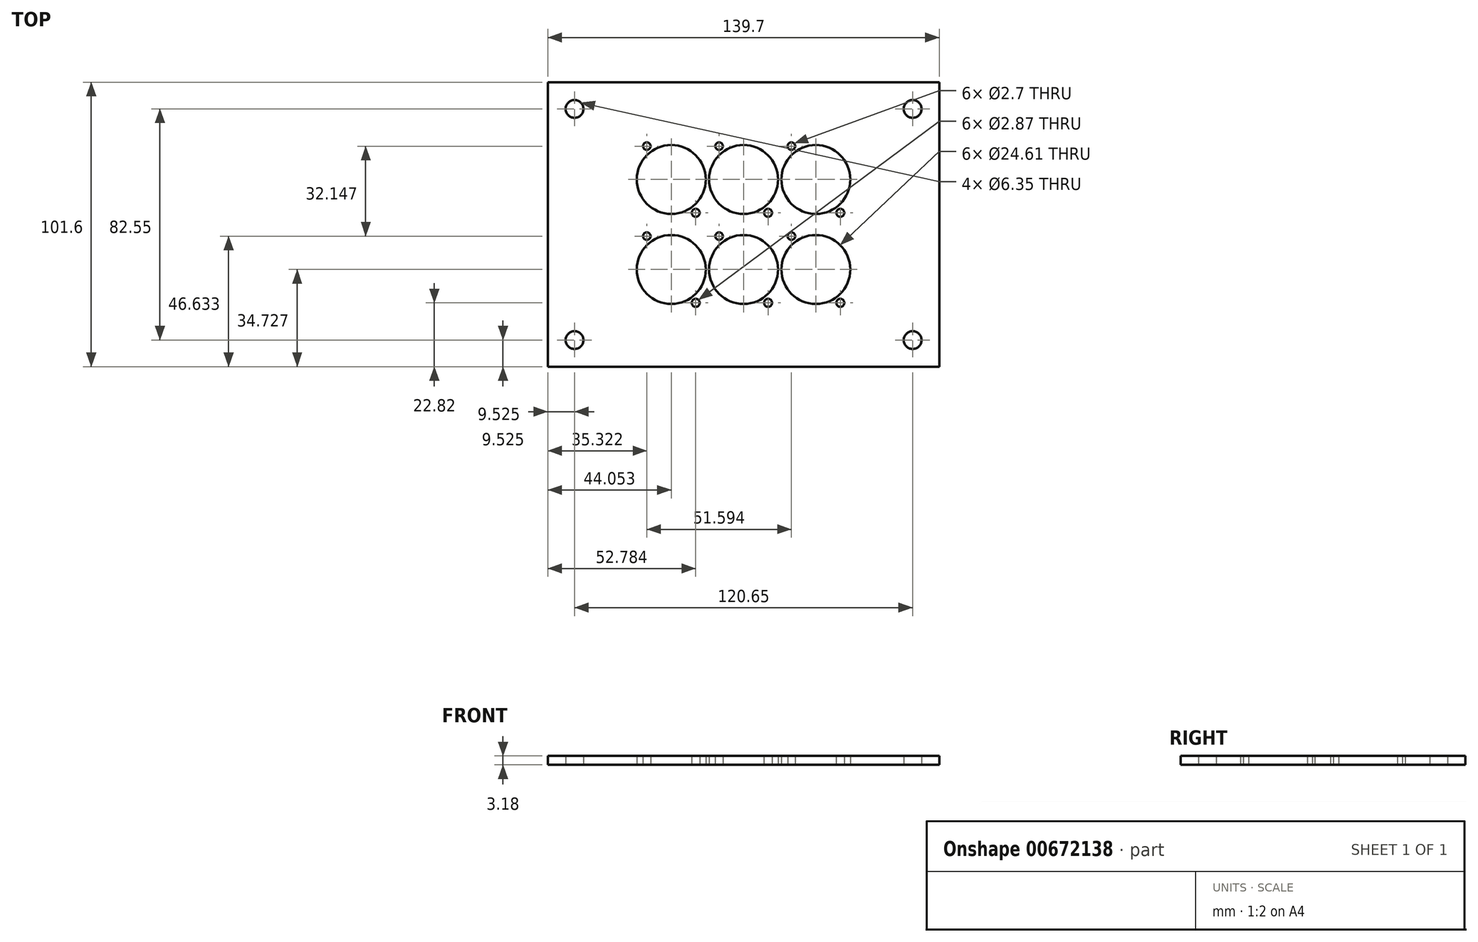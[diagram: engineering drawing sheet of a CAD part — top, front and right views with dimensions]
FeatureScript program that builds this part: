
annotation { "Feature Type Name" : "Feature", "Feature Type Description" : "" }
export const myFeature = defineFeature(function(context is Context, id is Id, definition is map)
    precondition{}
    {
        {
            var Q0;
            Q0=qCreatedBy(makeId("Top.planeOp"),FACE);
            var sketch = newSketch(context, id + "F0", { "sketchPlane" : qUnion([Q0])});
            skLineSegment(sketch, "E0.bottom", {"start": v(0, 0) * mm, "end": v(139.7, 0) * mm});
            skLineSegment(sketch, "E0.top", {"start": v(0, 101.6) * mm, "end": v(139.7, 101.6) * mm});
            skLineSegment(sketch, "E0.left", {"start": v(0, 0) * mm, "end": v(0, 101.6) * mm});
            skLineSegment(sketch, "E0.right", {"start": v(139.7, 0) * mm, "end": v(139.7, 101.6) * mm});
            skCircle(sketch, "E1", {"center": v(44.05, 66.87) * mm, "radius": 12.3 * mm});
            skCircle(sketch, "E2", {"center": v(130.18, 92.08) * mm, "radius": 3.18 * mm});
            skCircle(sketch, "E3", {"center": v(9.53, 92.08) * mm, "radius": 3.18 * mm});
            skCircle(sketch, "E4", {"center": v(9.53, 9.52) * mm, "radius": 3.18 * mm});
            skCircle(sketch, "E5", {"center": v(130.18, 9.53) * mm, "radius": 3.18 * mm});
            skLineSegment(sketch, "E6.bottom", {"start": v(56.75, 51) * mm, "end": v(31.35, 51) * mm});
            skLineSegment(sketch, "E6.top", {"start": v(56.75, 82.75) * mm, "end": v(31.35, 82.75) * mm});
            skLineSegment(sketch, "E6.left", {"start": v(56.75, 51) * mm, "end": v(56.75, 82.75) * mm});
            skLineSegment(sketch, "E6.right", {"start": v(31.35, 51) * mm, "end": v(31.35, 82.75) * mm});
            skCircle(sketch, "E7", {"center": v(35.32, 78.78) * mm, "radius": 1.35 * mm});
            skCircle(sketch, "E8", {"center": v(52.78, 54.97) * mm, "radius": 1.44 * mm});
            skLineSegment(sketch, "E9.0.1.0", {"start": v(56.75, 50.6) * mm, "end": v(31.35, 50.6) * mm});
            skLineSegment(sketch, "E9.0.1.1", {"start": v(56.75, 18.85) * mm, "end": v(56.75, 50.6) * mm});
            skLineSegment(sketch, "E9.0.1.2", {"start": v(31.35, 18.85) * mm, "end": v(31.35, 50.6) * mm});
            skPoint(sketch, "E9.0.1.3", {"position": v(44.05, 34.73) * mm});
            skCircle(sketch, "E9.0.1.4", {"center": v(44.05, 34.73) * mm, "radius": 12.3 * mm});
            skLineSegment(sketch, "E9.0.1.5", {"start": v(56.75, 18.85) * mm, "end": v(31.35, 18.85) * mm});
            skCircle(sketch, "E9.0.1.6", {"center": v(35.32, 46.63) * mm, "radius": 1.35 * mm});
            skCircle(sketch, "E9.0.1.7", {"center": v(52.78, 22.82) * mm, "radius": 1.44 * mm});
            skLineSegment(sketch, "E9.1.0.0", {"start": v(82.55, 82.75) * mm, "end": v(57.15, 82.75) * mm});
            skLineSegment(sketch, "E9.1.0.1", {"start": v(82.55, 51) * mm, "end": v(82.55, 82.75) * mm});
            skLineSegment(sketch, "E9.1.0.2", {"start": v(57.15, 51) * mm, "end": v(57.15, 82.75) * mm});
            skPoint(sketch, "E9.1.0.3", {"position": v(69.85, 66.87) * mm});
            skCircle(sketch, "E9.1.0.4", {"center": v(69.85, 66.87) * mm, "radius": 12.3 * mm});
            skLineSegment(sketch, "E9.1.0.5", {"start": v(82.55, 51) * mm, "end": v(57.15, 51) * mm});
            skCircle(sketch, "E9.1.0.6", {"center": v(61.12, 78.78) * mm, "radius": 1.35 * mm});
            skCircle(sketch, "E9.1.0.7", {"center": v(78.58, 54.97) * mm, "radius": 1.44 * mm});
            skLineSegment(sketch, "E9.1.1.0", {"start": v(82.55, 50.6) * mm, "end": v(57.15, 50.6) * mm});
            skLineSegment(sketch, "E9.1.1.1", {"start": v(82.55, 18.85) * mm, "end": v(82.55, 50.6) * mm});
            skLineSegment(sketch, "E9.1.1.2", {"start": v(57.15, 18.85) * mm, "end": v(57.15, 50.6) * mm});
            skPoint(sketch, "E9.1.1.3", {"position": v(69.85, 34.73) * mm});
            skCircle(sketch, "E9.1.1.4", {"center": v(69.85, 34.73) * mm, "radius": 12.3 * mm});
            skLineSegment(sketch, "E9.1.1.5", {"start": v(82.55, 18.85) * mm, "end": v(57.15, 18.85) * mm});
            skCircle(sketch, "E9.1.1.6", {"center": v(61.12, 46.63) * mm, "radius": 1.35 * mm});
            skCircle(sketch, "E9.1.1.7", {"center": v(78.58, 22.82) * mm, "radius": 1.44 * mm});
            skLineSegment(sketch, "E9.2.0.0", {"start": v(108.35, 82.75) * mm, "end": v(82.95, 82.75) * mm});
            skLineSegment(sketch, "E9.2.0.1", {"start": v(108.35, 51) * mm, "end": v(108.35, 82.75) * mm});
            skLineSegment(sketch, "E9.2.0.2", {"start": v(82.95, 51) * mm, "end": v(82.95, 82.75) * mm});
            skPoint(sketch, "E9.2.0.3", {"position": v(95.65, 66.87) * mm});
            skCircle(sketch, "E9.2.0.4", {"center": v(95.65, 66.87) * mm, "radius": 12.3 * mm});
            skLineSegment(sketch, "E9.2.0.5", {"start": v(108.35, 51) * mm, "end": v(82.95, 51) * mm});
            skCircle(sketch, "E9.2.0.6", {"center": v(86.92, 78.78) * mm, "radius": 1.35 * mm});
            skCircle(sketch, "E9.2.0.7", {"center": v(104.38, 54.97) * mm, "radius": 1.44 * mm});
            skLineSegment(sketch, "E9.2.1.0", {"start": v(108.35, 50.6) * mm, "end": v(82.95, 50.6) * mm});
            skLineSegment(sketch, "E9.2.1.1", {"start": v(108.35, 18.85) * mm, "end": v(108.35, 50.6) * mm});
            skLineSegment(sketch, "E9.2.1.2", {"start": v(82.95, 18.85) * mm, "end": v(82.95, 50.6) * mm});
            skPoint(sketch, "E9.2.1.3", {"position": v(95.65, 34.73) * mm});
            skCircle(sketch, "E9.2.1.4", {"center": v(95.65, 34.73) * mm, "radius": 12.3 * mm});
            skLineSegment(sketch, "E9.2.1.5", {"start": v(108.35, 18.85) * mm, "end": v(82.95, 18.85) * mm});
            skCircle(sketch, "E9.2.1.6", {"center": v(86.92, 46.63) * mm, "radius": 1.35 * mm});
            skCircle(sketch, "E9.2.1.7", {"center": v(104.38, 22.82) * mm, "radius": 1.44 * mm});
            skLineSegment(sketch, "E9.direction1", {"start": v(31.35, 51) * mm, "end": v(57.15, 51) * mm, "construction": true});
            skLineSegment(sketch, "E9.direction2", {"start": v(31.35, 51) * mm, "end": v(31.35, 18.85) * mm, "construction": true});
            skSolve(sketch);
        }
        {
            var Q0;
            Q0=makeQuery(id+"F0.imprint","IMPRINT",FACE,{"disambiguationData":[TD([[makeQuery(id+"F0.imprint","IMPRINT",EDGE,{"derivedFrom":sQuery(id+"F0.wireOp",EDGE,"E0.bottom")}),1.0]])]});
            var Q1;
            Q1=makeQuery(id+"F0.imprint","IMPRINT",FACE,{"disambiguationData":[TD([[makeQuery(id+"F0.imprint","IMPRINT",EDGE,{"derivedFrom":sQuery(id+"F0.wireOp",EDGE,"E1")}),-1.0]])]});
            var Q2;
            Q2=makeQuery(id+"F0.imprint","IMPRINT",FACE,{"disambiguationData":[TD([[makeQuery(id+"F0.imprint","IMPRINT",EDGE,{"derivedFrom":sQuery(id+"F0.wireOp",EDGE,"E9.1.0.0")}),1.0]])]});
            var Q3;
            Q3=makeQuery(id+"F0.imprint","IMPRINT",FACE,{"disambiguationData":[TD([[makeQuery(id+"F0.imprint","IMPRINT",EDGE,{"derivedFrom":sQuery(id+"F0.wireOp",EDGE,"E9.2.0.0")}),1.0]])]});
            var Q4;
            Q4=makeQuery(id+"F0.imprint","IMPRINT",FACE,{"disambiguationData":[TD([[makeQuery(id+"F0.imprint","IMPRINT",EDGE,{"derivedFrom":sQuery(id+"F0.wireOp",EDGE,"E9.2.1.0")}),1.0]])]});
            var Q5;
            Q5=makeQuery(id+"F0.imprint","IMPRINT",FACE,{"disambiguationData":[TD([[makeQuery(id+"F0.imprint","IMPRINT",EDGE,{"derivedFrom":sQuery(id+"F0.wireOp",EDGE,"E9.1.1.0")}),1.0]])]});
            var Q6;
            Q6=makeQuery(id+"F0.imprint","IMPRINT",FACE,{"disambiguationData":[TD([[makeQuery(id+"F0.imprint","IMPRINT",EDGE,{"derivedFrom":sQuery(id+"F0.wireOp",EDGE,"E9.0.1.0")}),1.0]])]});
            extrude(context, id + "F1", {"entities" : qUnion([Q0, Q1, Q2, Q3, Q4, Q5, Q6]), "depth" : 3.17 * mm, "offsetDistance" : 25.4 * mm});
        }
    });
